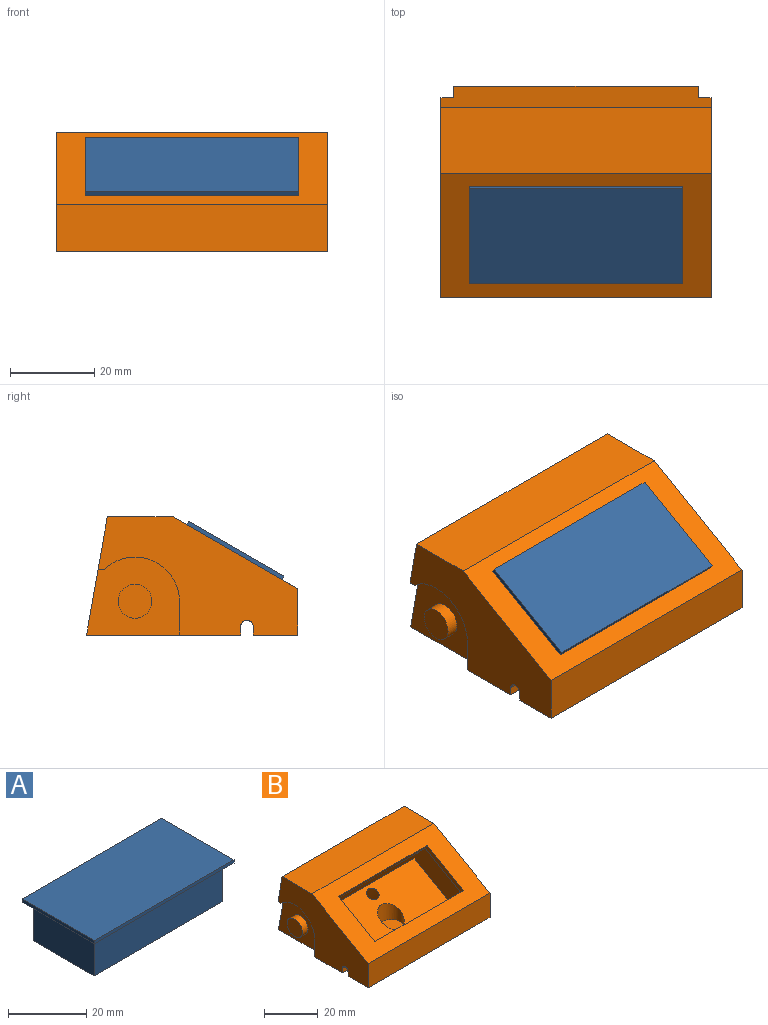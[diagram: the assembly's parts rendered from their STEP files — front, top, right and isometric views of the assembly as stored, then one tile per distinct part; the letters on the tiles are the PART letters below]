
ASSEMBLY  parts=2 mates=1
PART A: 11 faces, bbox 50.5x26x13 mm
  f0: plane 46.5x12mm, normal (0,1,0), area 558mm2, adj f1,f3,f4,f10
  f1: plane 22x12mm, normal (-1,0,0), area 264mm2, adj f0,f2,f4,f10
  f2: plane 46.5x12mm, normal (0,-1,0), area 558mm2, adj f1,f3,f4,f10
  f3: plane 22x12mm, normal (1,0,0), area 264mm2, adj f0,f2,f4,f10
  f4: plane 46.5x22mm, normal (0,0,-1), area 1023mm2, adj f0,f1,f2,f3
  f5: plane 50.5x1mm, normal (0,1,0), area 50.5mm2, adj f6,f8,f9,f10
  f6: plane 26x1mm, normal (-1,0,0), area 26mm2, adj f5,f7,f9,f10
  f7: plane 50.5x1mm, normal (0,-1,0), area 50.5mm2, adj f6,f8,f9,f10
  f8: plane 26x1mm, normal (1,0,0), area 26mm2, adj f5,f7,f9,f10
  f9: plane 50.5x26mm, normal (0,0,1), area 1313mm2, adj f5,f6,f7,f8
  f10: plane 50.5x26mm, normal (0,0,-1), area 290mm2, adj f0,f1,f2,f3,f5,f6,f7,f8
PART B: 37 faces, bbox 65.2x51.2x31.7 mm
  f0: plane 64x36.5mm, normal (0,0,-1), area 2181.3mm2, adj f1,f2,f9,f17,f24,f28,f30,f34
  f1: plane 64x28mm, normal (0,0.98,0.17), area 1724.6mm2, adj f0,f2,f7,f9,f26,f28,f31,f34
  f2: plane 47.25x28mm, normal (1,0,0), area 728.1mm2, adj f0,f1,f3,f4,f5,f6,f7,f8
  f3: cylinder r=1.5mm len=64mm, axis (-1,0,0), area 92.9mm2, adj f2,f4,f9,f14,f17,f19,f20
  f4: plane 64x2mm, normal (0,1,0), area 72.3mm2, adj f2,f3,f6,f9,f18,f19,f20
  f5: plane 64x29.45mm, normal (0,-0.5,0.87), area 1153mm2, adj f2,f7,f8,f9,f10,f11,f12,f13
  f6: plane 64x10.5mm, normal (0,0,-1), area 672mm2, adj f2,f4,f8,f9
  f7: plane 64x15.62mm, normal (0,0,1), area 999.6mm2, adj f1,f2,f5,f9
  f8: plane 64x11mm, normal (0,-1,0), area 704mm2, adj f2,f5,f6,f9
  f9: plane 47.25x28mm, normal (-1,0,0), area 728.1mm2, adj f0,f1,f3,f4,f5,f6,f7,f8
  f10: plane 46.5x1.73mm, normal (0,-0.87,-0.5), area 93mm2, adj f5,f11,f13,f21
  f11: plane 20.05x12.73mm, normal (1,0,0), area 44mm2, adj f5,f10,f12,f21
  f12: plane 46.5x1.73mm, normal (0,0.87,0.5), area 93mm2, adj f5,f11,f13,f21
  f13: plane 20.05x12.73mm, normal (-1,0,0), area 44mm2, adj f5,f10,f12,f21
  f14: plane 51.71x20.81mm, normal (0,-0.5,0.87), area 1032.1mm2, adj f3,f16,f19,f20,f22,f36
  f15: plane 10x10mm, normal (0,0,1), area 78.5mm2, adj f16
  f16: cylinder r=5mm len=10mm, axis (0,0,-1), area 156.4mm2, adj f14,f15
  f17: plane 64x2mm, normal (0,-1,0), area 128mm2, adj f0,f2,f3,f9
  f18: plane 50.5x0.04mm, normal (0,-0.5,0.87), area 2.1mm2, adj f4,f19,f20,f23
  f19: plane 28.52x23.39mm, normal (1,0,0), area 307.7mm2, adj f3,f4,f14,f18,f21,f22,f23
  f20: plane 28.52x23.39mm, normal (-1,0,0), area 307.7mm2, adj f3,f4,f14,f18,f21,f22,f23
  f21: plane 50.5x22.52mm, normal (0,0.5,-0.87), area 290mm2, adj f10,f11,f12,f13,f19,f20,f22,f23
  f22: plane 50.5x10.39mm, normal (0,-0.87,-0.5), area 606mm2, adj f14,f19,f20,f21
  f23: plane 50.5x10.39mm, normal (0,0.87,0.5), area 606mm2, adj f18,f19,f20,f21
  f24: plane 8x3mm, normal (0,1,0), area 24mm2, adj f0,f9,f25,f28
  f25: cylinder r=10.5mm len=17.75mm, axis (-1,0,0), area 73.5mm2, adj f9,f24,f26,f28
  f26: plane 3x1.5mm, normal (0,0,-1), area 4.5mm2, adj f1,f9,f25,f28
  f27: cylinder r=4mm len=8mm, axis (-1,0,0), area 75.4mm2, adj f28,f29
  f28: plane 22x18.5mm, normal (-1,0,0), area 292.7mm2, adj f0,f1,f24,f25,f26,f27
  f29: plane 8x8mm, normal (-1,0,0), area 50.3mm2, adj f27
  f30: plane 8x3mm, normal (0,1,0), area 24mm2, adj f0,f2,f32,f34
  f31: plane 3x1.5mm, normal (0,0,-1), area 4.5mm2, adj f1,f2,f32,f34
  f32: cylinder r=10.5mm len=17.75mm, axis (1,0,0), area 73.5mm2, adj f2,f30,f31,f34
  f33: cylinder r=4mm len=8mm, axis (1,0,0), area 75.4mm2, adj f34,f35
  f34: plane 22x18.5mm, normal (1,0,0), area 292.7mm2, adj f0,f1,f30,f31,f32,f33
  f35: plane 8x8mm, normal (1,0,0), area 50.3mm2, adj f33
  f36: cylinder r=2.5mm len=15.64mm, axis (0,-0.5,0.87), area 215.4mm2, adj f0,f14
PLACE A rot(axis=(1,0,0),30deg) t=(110.74,62.01,48.82)mm
PLACE B t=(-29.35,-67.29,0.12)mm fixed
MATE parallel A.f10 <-> B.f5  axis (0,0.5,-0.87) through (2.65,-12.3,19.78)mm
